# Revit family: Modular drawer
name_source: partatom
category: Installations électriques
units: mm (PartAtom-declared; Revit-internal decimal feet)

## family parameters
Basée sur le plan de construction = Non
Conserver l'orientation des annotations = Non
Cote de connecteur circulaire = Utiliser le diamètre
Couper avec des vides une fois chargée = Non
Partagée = Non
Point de calcul de pièce = Non
Toujours verticalement = Oui
Type d'élément = Normal

## types (1)
- 19 inches modular drawer 1U to be equipped
    BIM wording = 19 inches modular drawer 1U to be equipped
    Color = IDS_NOIR
    Depth = 334 mm
    E-catalogue link = https://www.legrand.fr
    EAN = 3414970961617
    ETIM class = EC001130
    Elévation par défaut = 0 mm  [stored 0 ft]
    Function = 19 inches modular optic drawer to be equipped with fibre optic blocks
    Height = 44 mm  [stored 0.144357 ft]
    IK = IK04
    Legrand part number = 032100
    Mounting method = 19 inches housing
    Number of height units = 1
    Operating temperature = -10°C à 60°C
    RAL Number = 9017
    Storage temperature = -10°C à 60°C
    Suitable for number of cassettes = 4
    Suitable for number of fibers = 96
    Width (mm) = 483 mm
    With front plate = Non
    With housing = Oui
    With label holder = Oui
    With pigtails = Non

note: [stored X ft] marks values corroborated as IEEE doubles in the binary element streams (Revit-internal decimal feet)
